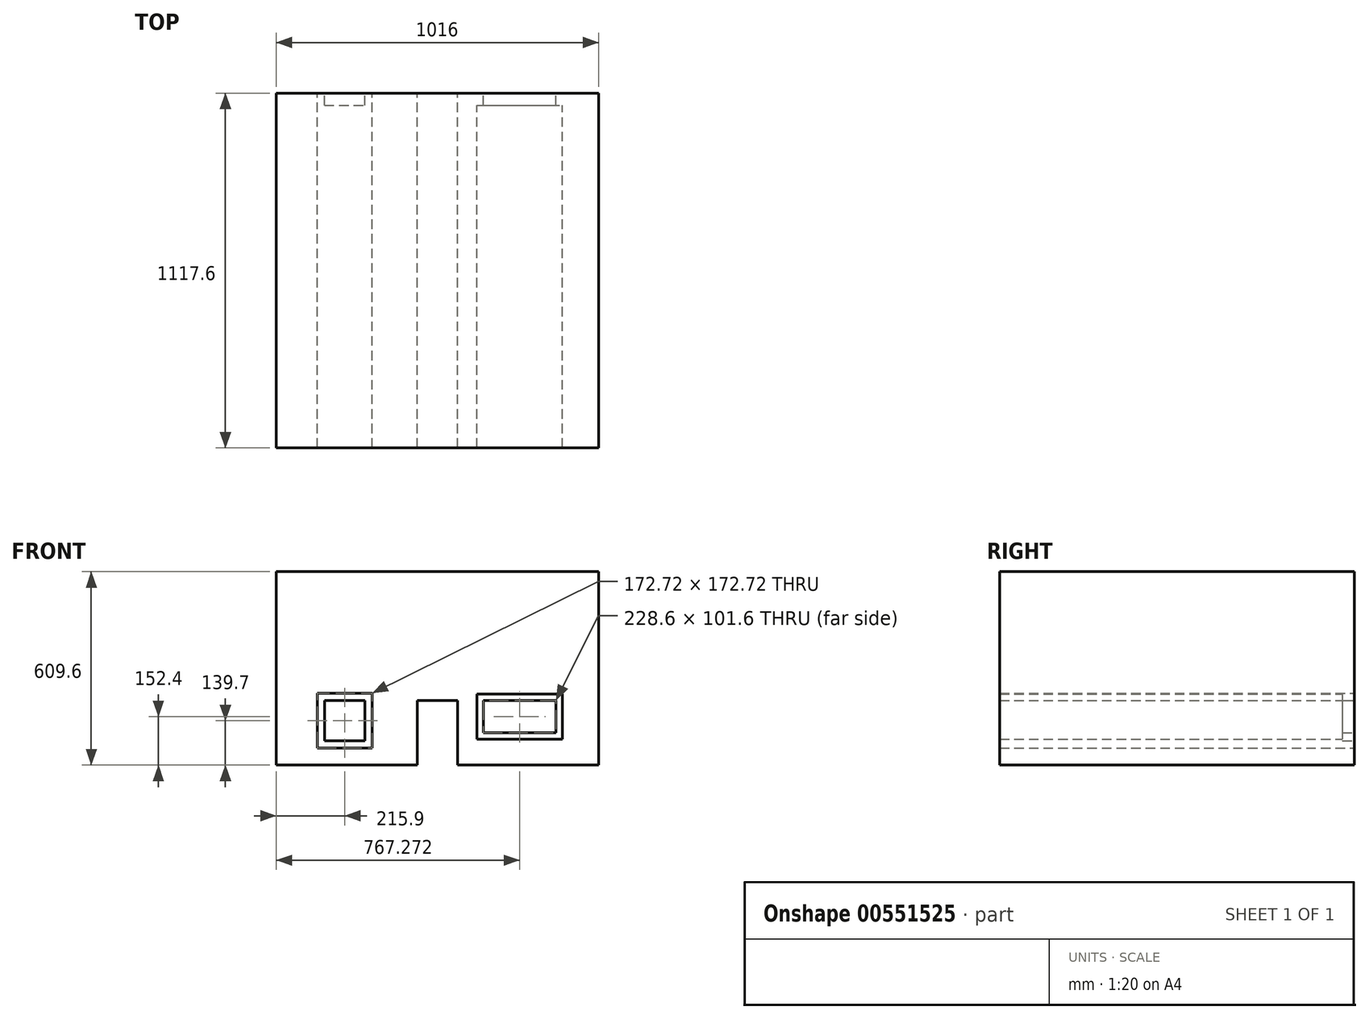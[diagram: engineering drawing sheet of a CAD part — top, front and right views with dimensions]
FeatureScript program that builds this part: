
annotation { "Feature Type Name" : "Feature", "Feature Type Description" : "" }
export const myFeature = defineFeature(function(context is Context, id is Id, definition is map)
    precondition{}
    {
        {
            var Q0;
            Q0=qCreatedBy(makeId("Front.planeOp"),FACE);
            var sketch = newSketch(context, id + "F0", { "sketchPlane" : qUnion([Q0])});
            skLineSegment(sketch, "E0", {"start": v(0, 0) * mm, "end": v(-508, 0) * mm});
            skLineSegment(sketch, "E1", {"start": v(0, 0) * mm, "end": v(508, 0) * mm});
            skLineSegment(sketch, "E2", {"start": v(0, 0) * mm, "end": v(0, 254) * mm, "construction": true});
            skLineSegment(sketch, "E3", {"start": v(0, 254) * mm, "end": v(508, 0) * mm});
            skLineSegment(sketch, "E4", {"start": v(-508, 0) * mm, "end": v(-584.2, 0) * mm});
            skLineSegment(sketch, "E5", {"start": v(508, 0) * mm, "end": v(584.2, 0) * mm});
            skLineSegment(sketch, "E6", {"start": v(0, 254) * mm, "end": v(0, 292.1) * mm});
            skLineSegment(sketch, "E7", {"start": v(-508, 0) * mm, "end": v(0, 254) * mm});
            skLineSegment(sketch, "E8", {"start": v(0, 292.1) * mm, "end": v(-584.2, 0) * mm});
            skLineSegment(sketch, "E9", {"start": v(0, 292.1) * mm, "end": v(584.2, 0) * mm});
            skLineSegment(sketch, "E10", {"start": v(-508, 0) * mm, "end": v(-508, -609.6) * mm});
            skLineSegment(sketch, "E11", {"start": v(508, 0) * mm, "end": v(508, -609.6) * mm});
            skLineSegment(sketch, "E12", {"start": v(-508, -609.6) * mm, "end": v(508, -609.6) * mm});
            skLineSegment(sketch, "E13", {"start": v(0, 0) * mm, "end": v(0, -648.69) * mm, "construction": true});
            skPoint(sketch, "E13.endSnap0", {"position": v(0, -609.6) * mm});
            skLineSegment(sketch, "E14", {"start": v(0, -609.6) * mm, "end": v(38.1, -609.6) * mm});
            skLineSegment(sketch, "E15", {"start": v(38.1, -609.6) * mm, "end": v(-67.57, -609.6) * mm});
            skLineSegment(sketch, "E16.bottom", {"start": v(144.97, -406.4) * mm, "end": v(373.57, -406.4) * mm});
            skLineSegment(sketch, "E16.top", {"start": v(144.97, -508) * mm, "end": v(373.57, -508) * mm});
            skLineSegment(sketch, "E16.left", {"start": v(144.97, -406.4) * mm, "end": v(144.97, -508) * mm});
            skLineSegment(sketch, "E16.right", {"start": v(373.57, -406.4) * mm, "end": v(373.57, -508) * mm});
            skLineSegment(sketch, "E17.0", {"start": v(124.65, -386.08) * mm, "end": v(393.9, -386.08) * mm});
            skLineSegment(sketch, "E17.1", {"start": v(124.65, -386.08) * mm, "end": v(124.65, -528.32) * mm});
            skLineSegment(sketch, "E17.2", {"start": v(124.65, -528.32) * mm, "end": v(393.9, -528.32) * mm});
            skLineSegment(sketch, "E17.3", {"start": v(393.9, -386.08) * mm, "end": v(393.9, -528.32) * mm});
            skLineSegment(sketch, "E18.bottom", {"start": v(-355.6, -406.4) * mm, "end": v(-228.6, -406.4) * mm});
            skLineSegment(sketch, "E18.top", {"start": v(-355.6, -533.4) * mm, "end": v(-228.6, -533.4) * mm});
            skLineSegment(sketch, "E18.left", {"start": v(-355.6, -406.4) * mm, "end": v(-355.6, -533.4) * mm});
            skLineSegment(sketch, "E18.right", {"start": v(-228.6, -406.4) * mm, "end": v(-228.6, -533.4) * mm});
            skLineSegment(sketch, "E19.0", {"start": v(-378.46, -383.54) * mm, "end": v(-378.46, -556.26) * mm});
            skLineSegment(sketch, "E19.1", {"start": v(-378.46, -383.54) * mm, "end": v(-205.74, -383.54) * mm});
            skLineSegment(sketch, "E19.2", {"start": v(-205.74, -383.54) * mm, "end": v(-205.74, -556.26) * mm});
            skLineSegment(sketch, "E19.3", {"start": v(-378.46, -556.26) * mm, "end": v(-205.74, -556.26) * mm});
            skLineSegment(sketch, "E20.bottom", {"start": v(-38.1, -431.8) * mm, "end": v(38.1, -431.8) * mm});
            skLineSegment(sketch, "E20.top", {"start": v(-38.1, -609.6) * mm, "end": v(38.1, -609.6) * mm});
            skLineSegment(sketch, "E20.left", {"start": v(-38.1, -431.8) * mm, "end": v(-38.1, -609.6) * mm});
            skLineSegment(sketch, "E20.right", {"start": v(38.1, -431.8) * mm, "end": v(38.1, -609.6) * mm});
            skLineSegment(sketch, "E21.0", {"start": v(-63.5, -406.4) * mm, "end": v(-63.5, -635) * mm});
            skLineSegment(sketch, "E21.1", {"start": v(-63.5, -406.4) * mm, "end": v(63.5, -406.4) * mm});
            skLineSegment(sketch, "E21.2", {"start": v(63.5, -406.4) * mm, "end": v(63.5, -635) * mm});
            skLineSegment(sketch, "E21.3", {"start": v(-63.5, -635) * mm, "end": v(63.5, -635) * mm});
            skSolve(sketch);
        }
        {
            var Q0;
            Q0=sQuery(id+"F0.wireOp",EDGE,"E8");
            var Q1;
            Q1=sQuery(id+"F0.wireOp",EDGE,"E7");
            var Q2;
            Q2=sQuery(id+"F0.wireOp",EDGE,"E3");
            var Q3;
            Q3=sQuery(id+"F0.wireOp",EDGE,"E9");
            extrude(context, id + "F1", {"bodyType" : ToolBodyType.SURFACE, "surfaceEntities" : qUnion([Q0, Q1, Q2, Q3]), "depth" : 1117.6 * mm, "offsetDistance" : 25.4 * mm});
        }
        {
            var Q0;
            Q0=makeQuery(id+"F0.imprint","IMPRINT",FACE,{"disambiguationData":[TD([[makeQuery(id+"F0.imprint","IMPRINT",EDGE,{"derivedFrom":sQuery(id+"F0.wireOp",EDGE,"E0")}),1.0]])]});
            extrude(context, id + "F2", {"entities" : qUnion([Q0]), "depth" : 1117.6 * mm, "offsetDistance" : 25.4 * mm});
        }
        {
            var Q0;
            Q0=makeQuery(id+"F0.imprint","IMPRINT",FACE,{"disambiguationData":[TD([[makeQuery(id+"F0.imprint","IMPRINT",EDGE,{"derivedFrom":sQuery(id+"F0.wireOp",EDGE,"E16.bottom")}),1.0]])]});
            var Q1;
            Q1=makeQuery(id+"F0.imprint","IMPRINT",FACE,{"disambiguationData":[TD([[makeQuery(id+"F0.imprint","IMPRINT",EDGE,{"derivedFrom":sQuery(id+"F0.wireOp",EDGE,"E18.bottom")}),-1.0]])]});
            extrude(context, id + "F3", {"entities" : qUnion([Q0, Q1]), "operationType" : NewBodyOperationType.ADD, "depth" : 38.1 * mm, "offsetDistance" : 25.4 * mm});
        }
    });
